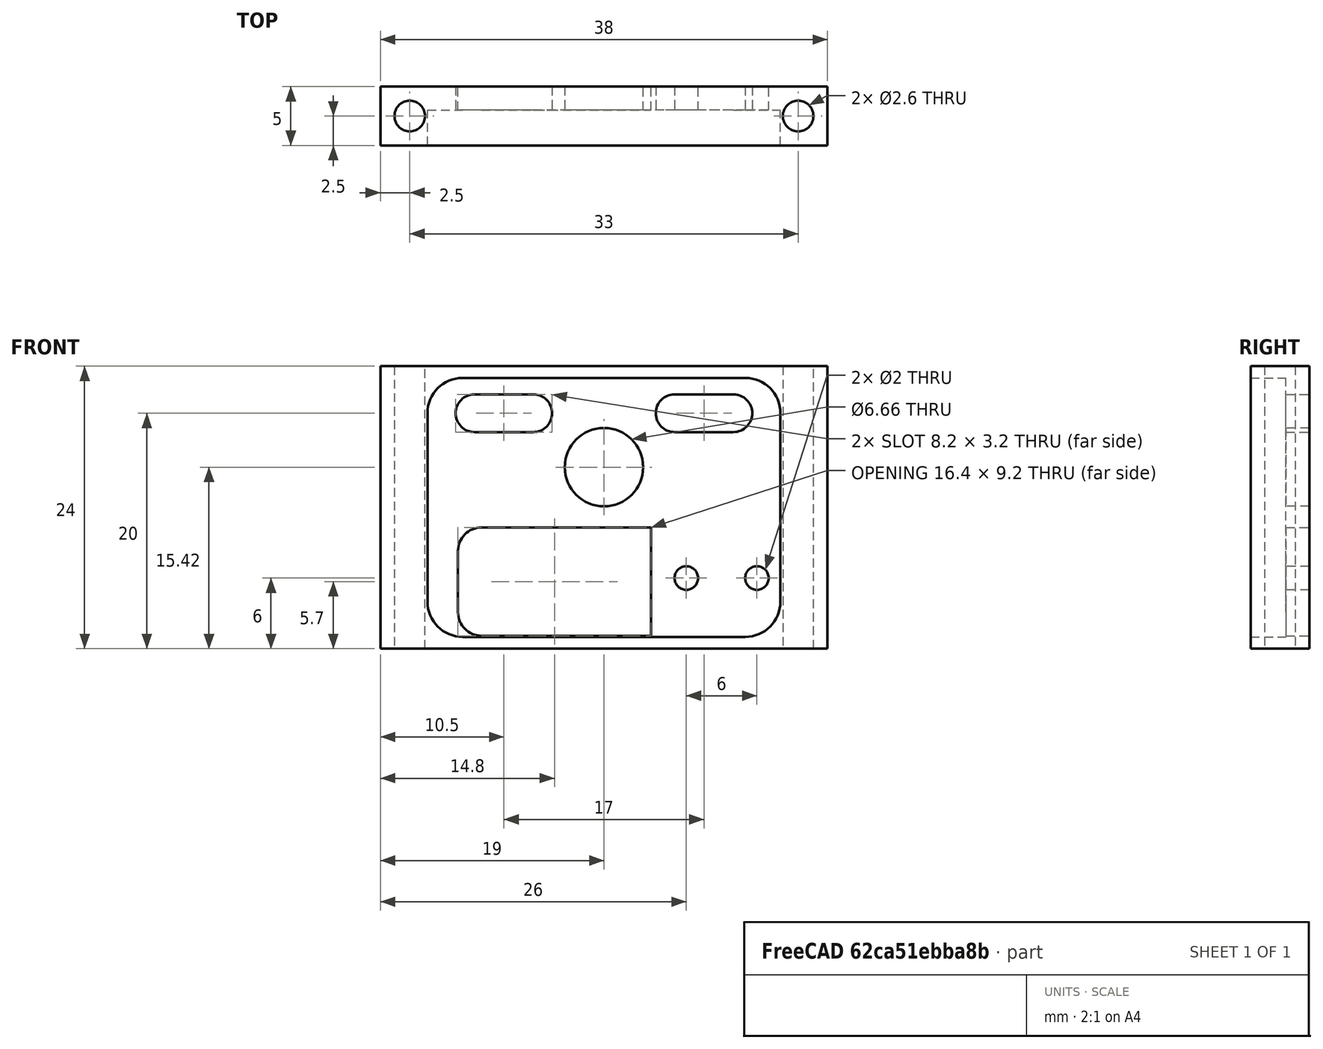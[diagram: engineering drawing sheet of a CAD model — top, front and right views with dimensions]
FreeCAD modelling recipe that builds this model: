
FCSTD DOCUMENT  (FreeCAD 0.18RUnknown)
Label: tail
License: All rights reserved
LicenseURL: http://en.wikipedia.org/wiki/All_rights_reserved
objects: TechDraw::DrawViewDimension×7, Sketcher::SketchObject×3, PartDesign::Pocket×2, TechDraw::DrawProjGroupItem×2, PartDesign::Pad×1, PartDesign::Body×1, TechDraw::DrawSVGTemplate×1, TechDraw::DrawProjGroup×1, TechDraw::DrawPage×1
note: 10 computed .brp shape members not serialized (recipe doc carries the construction recipe); baked Part::Feature solids carry a one-line shape summary decoded from their .brp

FEATURE [Sketcher::SketchObject] Sketch
  MapMode = 5
  Support = -> [XY_Plane]
  expr: Constraints[14] = anomaly#Spreadsheet.m3taper
  expr: Constraints[9] = anomaly#Spreadsheet.aluWidth
  expr: Constraints[16] = anomaly#Spreadsheet.aluHoleDist
  expr: Constraints[8] = anomaly#Spreadsheet.bodyWidth
  sketch-geometry (6):
    g0: LineSegment StartX=-19 StartY=2.5 StartZ=0 EndX=19 EndY=2.5 EndZ=0
    g1: LineSegment StartX=19 StartY=2.5 StartZ=0 EndX=19 EndY=-2.5 EndZ=0
    g2: LineSegment StartX=19 StartY=-2.5 StartZ=0 EndX=-19 EndY=-2.5 EndZ=0
    g3: LineSegment StartX=-19 StartY=-2.5 StartZ=0 EndX=-19 EndY=2.5 EndZ=0
    g4: Circle CenterX=-16.5 CenterY=0 CenterZ=0 NormalX=0 NormalY=0 NormalZ=1 AngleXU=0 Radius=1.3
    g5: Circle CenterX=16.5 CenterY=0 CenterZ=0 NormalX=0 NormalY=0 NormalZ=1 AngleXU=0 Radius=1.3
  constraints (18):
    c: Coincident(g0,g1)
    c: Coincident(g1,g2)
    c: Coincident(g2,g3)
    c: Coincident(g3,g0)
    c: Horizontal(g0)
    c: Horizontal(g2)
    c: Vertical(g1)
    c: Vertical(g3)
    c: DistanceX(g0,g0) = 38
    c: DistanceY(g1,g0) = 5
    c: Symmetric(g0,g1,g-1)
    c: Symmetric(g0,g2,g-1)
    c: PointOnObject(g4,g-1)
    c: PointOnObject(g5,g-1)
    c: Radius(g4) = 1.3
    c: Equal(g4,g5)
    c: DistanceX(g4,g5) = 33
    c: Symmetric(g4,g5,g-1)
FEATURE [PartDesign::Pad] Pad
  Length = 24
  Length2 = 100
  Midplane = true
  Profile = -> Sketch
  Type = 0
  expr: Length = anomaly#Spreadsheet.aluHeight
FEATURE [Sketcher::SketchObject] Sketch001
  MapMode = 5
  Placement = pos=(0,-2.5,0) rot=(1,0,0;1.5708rad)
  Support = -> [Pad]
  sketch-geometry (25):
    g0: Circle CenterX=0 CenterY=3.42 CenterZ=0 NormalX=0 NormalY=0 NormalZ=1 AngleXU=0 Radius=3.33
    g1: LineSegment [constr] StartX=-12.4 StartY=-1.7 StartZ=0 EndX=4 EndY=-1.7 EndZ=0
    g2: LineSegment [constr] StartX=4 StartY=-1.7 StartZ=0 EndX=4 EndY=-10.9 EndZ=0
    g3: LineSegment [constr] StartX=4 StartY=-10.9 StartZ=0 EndX=-12.4 EndY=-10.9 EndZ=0
    g4: LineSegment [constr] StartX=-12.4 StartY=-10.9 StartZ=0 EndX=-12.4 EndY=-1.7 EndZ=0
    g5: LineSegment StartX=4 StartY=-1.7 StartZ=0 EndX=-10.4 EndY=-1.7 EndZ=0
    g6: LineSegment StartX=-10.4 StartY=-10.9 StartZ=0 EndX=4 EndY=-10.9 EndZ=0
    g7: LineSegment StartX=4 StartY=-10.9 StartZ=0 EndX=4 EndY=-1.7 EndZ=0
    g8: Circle [constr] CenterX=0 CenterY=3.42 CenterZ=0 NormalX=0 NormalY=0 NormalZ=1 AngleXU=0 Radius=5
    g9: Circle [constr] CenterX=10 CenterY=-6 CenterZ=0 NormalX=0 NormalY=0 NormalZ=1 AngleXU=0 Radius=5
    g10: Circle CenterX=7 CenterY=-6 CenterZ=0 NormalX=0 NormalY=0 NormalZ=1 AngleXU=0 Radius=1
    g11: Circle CenterX=13 CenterY=-6 CenterZ=0 NormalX=0 NormalY=0 NormalZ=1 AngleXU=0 Radius=1
    g12: LineSegment [constr] StartX=7 StartY=-6 StartZ=0 EndX=10 EndY=-6 EndZ=0
    g13: LineSegment [constr] StartX=10 StartY=-6 StartZ=0 EndX=13 EndY=-6 EndZ=0
    g14: LineSegment StartX=-12.4 StartY=-3.7 StartZ=0 EndX=-12.4 EndY=-8.9 EndZ=0
    g15: ArcOfCircle CenterX=-10.4 CenterY=-3.7 CenterZ=0 NormalX=0 NormalY=0 NormalZ=1 AngleXU=0 Radius=2 StartAngle=1.5708 EndAngle=3.14159
    g16: ArcOfCircle CenterX=-10.4 CenterY=-8.9 CenterZ=0 NormalX=0 NormalY=0 NormalZ=1 AngleXU=0 Radius=2 StartAngle=3.14159 EndAngle=4.71239
    g17: ArcOfCircle CenterX=-11 CenterY=8 CenterZ=0 NormalX=0 NormalY=0 NormalZ=1 AngleXU=0 Radius=1.6 StartAngle=1.5708 EndAngle=4.71239
    g18: ArcOfCircle CenterX=-6 CenterY=8 CenterZ=0 NormalX=0 NormalY=0 NormalZ=1 AngleXU=0 Radius=1.6 StartAngle=4.71239 EndAngle=7.85398
    g19: LineSegment StartX=-11 StartY=6.4 StartZ=0 EndX=-6 EndY=6.4 EndZ=0
    g20: LineSegment StartX=-11 StartY=9.6 StartZ=0 EndX=-6 EndY=9.6 EndZ=0
    g21: ArcOfCircle CenterX=6 CenterY=8 CenterZ=0 NormalX=0 NormalY=0 NormalZ=1 AngleXU=0 Radius=1.6 StartAngle=1.5708 EndAngle=4.71239
    g22: ArcOfCircle CenterX=11 CenterY=8 CenterZ=0 NormalX=0 NormalY=0 NormalZ=1 AngleXU=0 Radius=1.6 StartAngle=4.71239 EndAngle=7.85398
    g23: LineSegment StartX=6 StartY=6.4 StartZ=0 EndX=11 EndY=6.4 EndZ=0
    g24: LineSegment StartX=6 StartY=9.6 StartZ=0 EndX=11 EndY=9.6 EndZ=0
  constraints (63):
    c: Radius(g0) = 3.33
    c: Coincident(g1,g2)
    c: Coincident(g2,g3)
    c: Coincident(g3,g4)
    c: Coincident(g4,g1)
    c: Horizontal(g1)
    c: Horizontal(g3)
    c: Vertical(g2)
    c: Vertical(g4)
    c: DistanceY(g2,g1) = 9.2
    c: DistanceX(g1,g1) = 16.4
    c: Coincident(g5,g1)
    c: Horizontal(g5)
    c: Coincident(g6,g2)
    c: Coincident(g7,g2)
    c: Coincident(g7,g1)
    c: Coincident(g8,g0)
    c: Coincident(g12,g10)
    c: Coincident(g12,g9)
    c: Horizontal(g12)
    c: Coincident(g13,g9)
    c: Coincident(g13,g11)
    c: Horizontal(g13)
    c: DistanceX(g10,g11) = 6
    c: Radius(g9) = 5
    c: Tangent(g5,g15) = -1.5708
    c: Tangent(g14,g15) = -1.5708
    c: Tangent(g14,g16) = -1.5708
    c: Tangent(g6,g16) = -1.5708
    c: Equal(g15,g16)
    c: PointOnObject(g14,g4)
    c: PointOnObject(g14,g4)
    c: PointOnObject(g6,g3)
    c: Radius(g15) = 2
    c: Tangent(g17,g20) = 1.5708
    c: Tangent(g17,g19) = -1.5708
    c: Tangent(g19,g18) = -1.5708
    c: Tangent(g20,g18) = 1.5708
    c: Horizontal(g19)
    c: Equal(g17,g18)
    c: Tangent(g21,g24) = 1.5708
    c: Tangent(g21,g23) = -1.5708
    c: Tangent(g23,g22) = -1.5708
    c: Tangent(g24,g22) = 1.5708
    c: Horizontal(g23)
    c: Equal(g21,g22)
    c: Equal(g18,g22)
    c: DistanceX(g18,g21) = 12
    c: Equal(g24,g20)
    c: Symmetric(g18,g21,g-2)
    c: DistanceY(g-1,g18) = 8
    c: Radius(g17) = 1.6
    c: DistanceX(g17,g22) = 22
    c: Symmetric(g10,g11,g9)
    c: PointOnObject(g0,g-2)
    c: DistanceY(g15,g-1) = 3.7
    c: Radius(g10) = 1
    c: Equal(g10,g11)
    c: DistanceY(g9) = -6
    c: DistanceX(g-1,g1) = 4
    c: Radius(g8) = 5
    c: DistanceY(g-1,g0) = 3.42
    c: DistanceX(g-1,g9) = 10
FEATURE [PartDesign::Pocket] Pocket
  BaseFeature = -> Pad
  Length = 5
  Length2 = 100
  Profile = -> Sketch001
  Type = 1
FEATURE [Sketcher::SketchObject] Sketch002
  MapMode = 5
  Placement = pos=(0,-2.5,0) rot=(1,0,0;1.5708rad)
  Support = -> [Pocket]
  sketch-geometry (8):
    g0: LineSegment StartX=-12 StartY=11 StartZ=0 EndX=12 EndY=11 EndZ=0
    g1: LineSegment StartX=15 StartY=8 StartZ=0 EndX=15 EndY=-8 EndZ=0
    g2: LineSegment StartX=12 StartY=-11 StartZ=0 EndX=-12 EndY=-11 EndZ=0
    g3: LineSegment StartX=-15 StartY=-8 StartZ=0 EndX=-15 EndY=8 EndZ=0
    g4: ArcOfCircle CenterX=-12 CenterY=8 CenterZ=0 NormalX=0 NormalY=0 NormalZ=1 AngleXU=0 Radius=3 StartAngle=1.5708 EndAngle=3.14159
    g5: ArcOfCircle CenterX=-12 CenterY=-8 CenterZ=0 NormalX=0 NormalY=0 NormalZ=1 AngleXU=0 Radius=3 StartAngle=3.14159 EndAngle=4.71239
    g6: ArcOfCircle CenterX=12 CenterY=-8 CenterZ=0 NormalX=0 NormalY=0 NormalZ=1 AngleXU=0 Radius=3 StartAngle=4.71239 EndAngle=6.28319
    g7: ArcOfCircle CenterX=12 CenterY=8 CenterZ=0 NormalX=0 NormalY=0 NormalZ=1 AngleXU=0 Radius=3 StartAngle=0 EndAngle=1.5708
  constraints (19):
    c: Horizontal(g0)
    c: Horizontal(g2)
    c: Vertical(g1)
    c: Vertical(g3)
    c: Tangent(g0,g4) = 1.5708
    c: Tangent(g3,g4) = 1.5708
    c: Tangent(g3,g5) = 1.5708
    c: Tangent(g2,g5) = 1.5708
    c: Tangent(g1,g6) = 1.5708
    c: Tangent(g2,g6) = 1.5708
    c: Tangent(g1,g7) = 1.5708
    c: Tangent(g0,g7) = 1.5708
    c: Equal(g4,g5)
    c: Equal(g5,g6)
    c: Equal(g6,g7)
    c: Symmetric(g6,g4,g-1)
    c: DistanceY(g2,g0) = 22
    c: DistanceX(g3,g1) = 30
    c: Radius(g7) = 3
FEATURE [PartDesign::Pocket] Pocket001
  BaseFeature = -> Pocket
  Length = 3
  Length2 = 100
  Profile = -> Sketch002
  Type = 0
FEATURE [PartDesign::Body] Body
  Group = -> [Sketch,Pad,Sketch001,Pocket,Sketch002,Pocket001]
  Origin = -> Origin
  Tip = -> Pocket001
FEATURE [TechDraw::DrawSVGTemplate] Template
  EditableTexts = Designed_by_Name=Designed by Name; Drawing_number=Drawing number; FC-Date=Date; FC-SC=Scale; FC-SH=Sheet; FC-Title=Title; Subtitle=tail; Weight=Weight
  Height = 210
  Orientation = 1
  Width = 297
FEATURE [TechDraw::DrawProjGroupItem] ProjItem  label="Front"
  CoarseView = false
  Direction = (0,-1,0)
  Focus = 100
  HardHidden = false
  IsoCount = 0
  IsoHidden = false
  IsoVisible = false
  LockPosition = false
  Perspective = false
  Rotation = 0
  RotationVector = (1,0,0)
  ScaleType = 0
  SeamHidden = false
  SeamVisible = false
  SmoothHidden = false
  SmoothVisible = false
  Source = -> [Pocket001]
  Type = 0
  X = 0
  Y = 0
FEATURE [TechDraw::DrawProjGroupItem] ProjItem001  label="Top"
  CoarseView = false
  Direction = (0,0,1)
  Focus = 100
  HardHidden = false
  IsoCount = 0
  IsoHidden = false
  IsoVisible = false
  LockPosition = false
  Perspective = false
  Rotation = 0
  RotationVector = (1,0,0)
  ScaleType = 0
  SeamHidden = false
  SeamVisible = false
  SmoothHidden = false
  SmoothVisible = false
  Source = -> [Pocket001]
  Type = 4
  X = 0
  Y = -87
FEATURE [TechDraw::DrawProjGroup] ProjGroup
  Anchor = -> ProjItem
  AutoDistribute = true
  LockPosition = false
  ProjectionType = 0
  Rotation = 0
  Scale = 3
  ScaleType = 2
  Source = -> [Pocket001]
  Views = -> [ProjItem,ProjItem001]
  X = 82.4773
  Y = 147.689
  spacingX = 15
  spacingY = 15
FEATURE [TechDraw::DrawViewDimension] Dimension
  Arbitrary = false
  FormatSpec = %.2f
  LockPosition = false
  MeasureType = 1
  OverTolerance = 0
  References2D = -> [ProjItem001]
  Rotation = 0
  ScaleType = 0
  Type = 1
  UnderTolerance = 0
  X = -1.61366
  Y = 25.6169
FEATURE [TechDraw::DrawViewDimension] Dimension001
  Arbitrary = false
  FormatSpec = %.2f
  LockPosition = false
  MeasureType = 1
  OverTolerance = 0
  References2D = -> [ProjItem001]
  Rotation = 0
  ScaleType = 0
  Type = 1
  UnderTolerance = 0
  X = 86.936
  Y = 19.1622
FEATURE [TechDraw::DrawViewDimension] Dimension002
  Arbitrary = false
  FormatSpec = %.2f
  LockPosition = false
  MeasureType = 1
  OverTolerance = 0
  References2D = -> [ProjItem001]
  Rotation = 0
  ScaleType = 0
  Type = 2
  UnderTolerance = 0
  X = 56.5551
  Y = -26.3148
FEATURE [TechDraw::DrawViewDimension] Dimension003
  Arbitrary = false
  FormatSpec = %.2f
  LockPosition = false
  MeasureType = 1
  OverTolerance = 0
  References2D = -> [ProjItem]
  Rotation = 0
  ScaleType = 0
  Type = 1
  UnderTolerance = 0
  X = 32.1466
  Y = -48.4372
FEATURE [TechDraw::DrawViewDimension] Dimension004
  Arbitrary = false
  FormatSpec = %.2f
  LockPosition = false
  MeasureType = 1
  OverTolerance = 0
  References2D = -> [ProjItem]
  Rotation = 0
  ScaleType = 0
  Type = 1
  UnderTolerance = 0
  X = 47.8746
  Y = -40.141
FEATURE [TechDraw::DrawViewDimension] Dimension005
  Arbitrary = false
  FormatSpec = %.2f
  LockPosition = false
  MeasureType = 1
  OverTolerance = 0
  References2D = -> [ProjItem]
  Rotation = 0
  ScaleType = 0
  Type = 2
  UnderTolerance = 0
  X = 71.6073
  Y = -5.75416
FEATURE [TechDraw::DrawViewDimension] Dimension006
  Arbitrary = false
  FormatSpec = %.2f
  LockPosition = false
  MeasureType = 1
  OverTolerance = 0
  References2D = -> [ProjItem001]
  Rotation = 0
  ScaleType = 0
  Type = 1
  UnderTolerance = 0
  X = 0.795455
  Y = -23.3333
FEATURE [TechDraw::DrawPage] Page
  KeepUpdated = true
  ProjectionType = 0
  Template = -> Template
  Views = -> [ProjGroup,Dimension,Dimension001,Dimension002,Dimension003,Dimension004,Dimension005,Dimension006]
